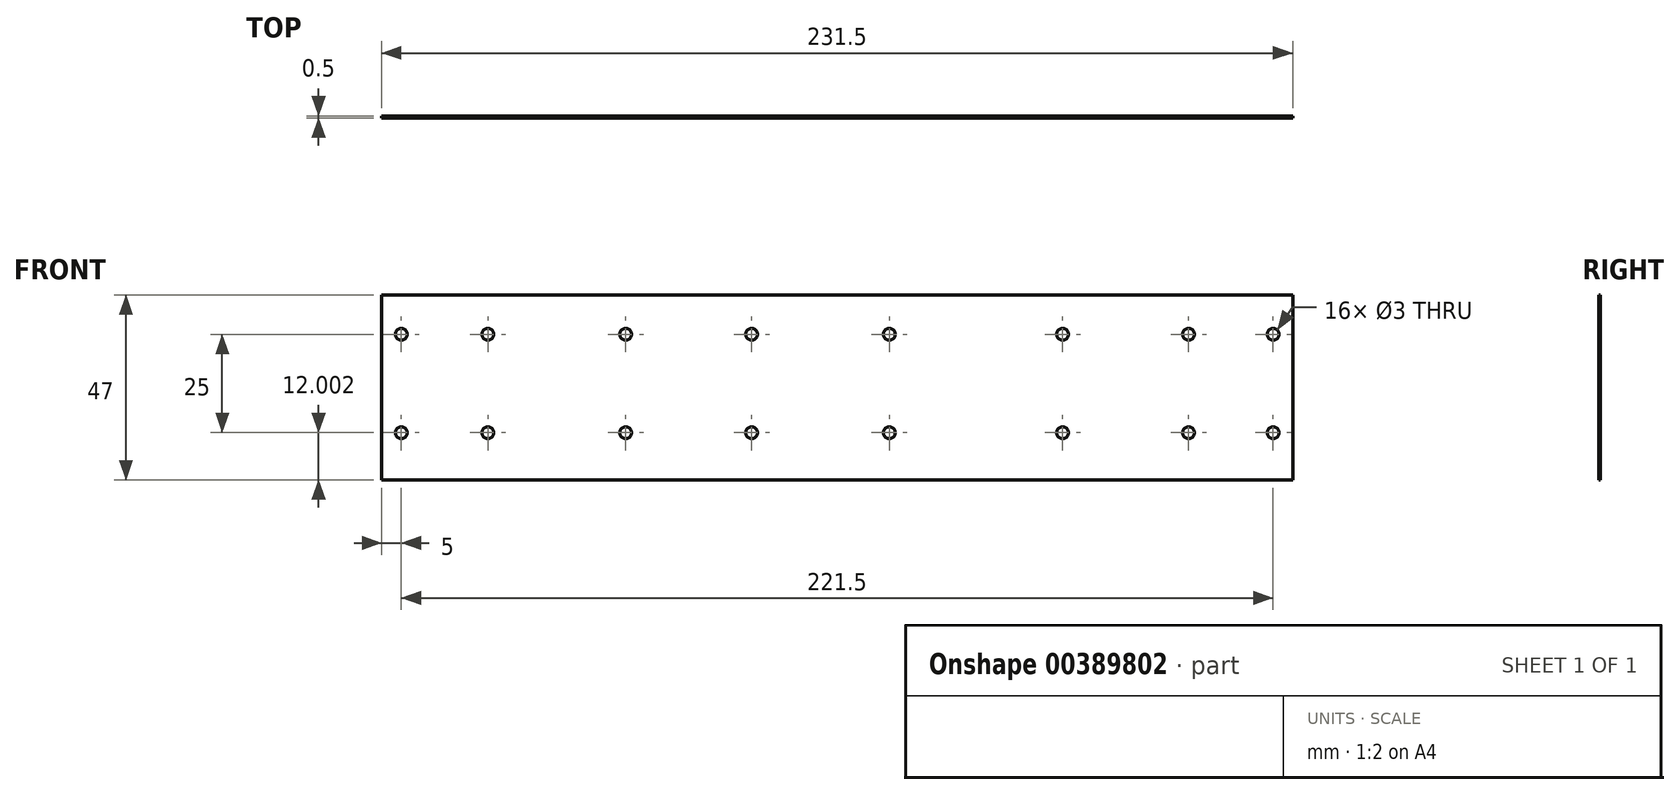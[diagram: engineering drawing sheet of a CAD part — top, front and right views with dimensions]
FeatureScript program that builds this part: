
annotation { "Feature Type Name" : "Feature", "Feature Type Description" : "" }
export const myFeature = defineFeature(function(context is Context, id is Id, definition is map)
    precondition{}
    {
        {
            var Q0;
            Q0=qCreatedBy(makeId("Front.planeOp"),FACE);
            var sketch = newSketch(context, id + "F0", { "sketchPlane" : qUnion([Q0])});
            skLineSegment(sketch, "E0.bottom", {"start": v(-56.37, 33.42) * mm, "end": v(175.13, 33.42) * mm});
            skLineSegment(sketch, "E0.top", {"start": v(-56.37, -13.58) * mm, "end": v(175.13, -13.58) * mm});
            skLineSegment(sketch, "E0.left", {"start": v(-56.37, 33.42) * mm, "end": v(-56.37, -13.58) * mm});
            skLineSegment(sketch, "E0.right", {"start": v(175.13, 33.42) * mm, "end": v(175.13, -13.58) * mm});
            skLineSegment(sketch, "E1", {"start": v(99.63, 33.42) * mm, "end": v(99.63, -13.58) * mm});
            skLineSegment(sketch, "E2", {"start": v(165.13, 33.42) * mm, "end": v(165.13, -13.58) * mm});
            skLineSegment(sketch, "E3", {"start": v(54.63, 33.42) * mm, "end": v(54.63, -13.58) * mm});
            skLineSegment(sketch, "E4", {"start": v(-11.37, 33.42) * mm, "end": v(-11.37, -13.58) * mm});
            skCircle(sketch, "E5", {"center": v(170.13, 23.42) * mm, "radius": 1.5 * mm});
            skCircle(sketch, "E6", {"center": v(170.13, -1.58) * mm, "radius": 1.5 * mm});
            skCircle(sketch, "E7", {"center": v(-51.37, 23.42) * mm, "radius": 1.5 * mm});
            skCircle(sketch, "E8", {"center": v(-51.37, -1.58) * mm, "radius": 1.5 * mm});
            skCircle(sketch, "E9", {"center": v(5.63, -1.58) * mm, "radius": 1.5 * mm});
            skCircle(sketch, "E10", {"center": v(37.63, -1.58) * mm, "radius": 1.5 * mm});
            skCircle(sketch, "E11", {"center": v(116.63, -1.58) * mm, "radius": 1.5 * mm});
            skCircle(sketch, "E12", {"center": v(148.63, -1.58) * mm, "radius": 1.5 * mm});
            skCircle(sketch, "E13", {"center": v(5.63, 23.42) * mm, "radius": 1.5 * mm});
            skCircle(sketch, "E14", {"center": v(37.63, 23.42) * mm, "radius": 1.5 * mm});
            skCircle(sketch, "E15", {"center": v(116.63, 23.42) * mm, "radius": 1.5 * mm});
            skCircle(sketch, "E16", {"center": v(148.63, 23.42) * mm, "radius": 1.5 * mm});
            skCircle(sketch, "E17", {"center": v(-29.37, 23.42) * mm, "radius": 1.5 * mm});
            skCircle(sketch, "E18", {"center": v(-29.37, -1.58) * mm, "radius": 1.5 * mm});
            skCircle(sketch, "E19", {"center": v(72.63, 23.42) * mm, "radius": 1.5 * mm});
            skCircle(sketch, "E20", {"center": v(72.63, -1.58) * mm, "radius": 1.5 * mm});
            skSolve(sketch);
        }
        {
            var Q0;
            Q0 = qSketchRegion(id + "F0", true);
            extrude(context, id + "F1", {"entities" : qUnion([Q0]), "depth" : 0.5 * mm});
        }
    });
